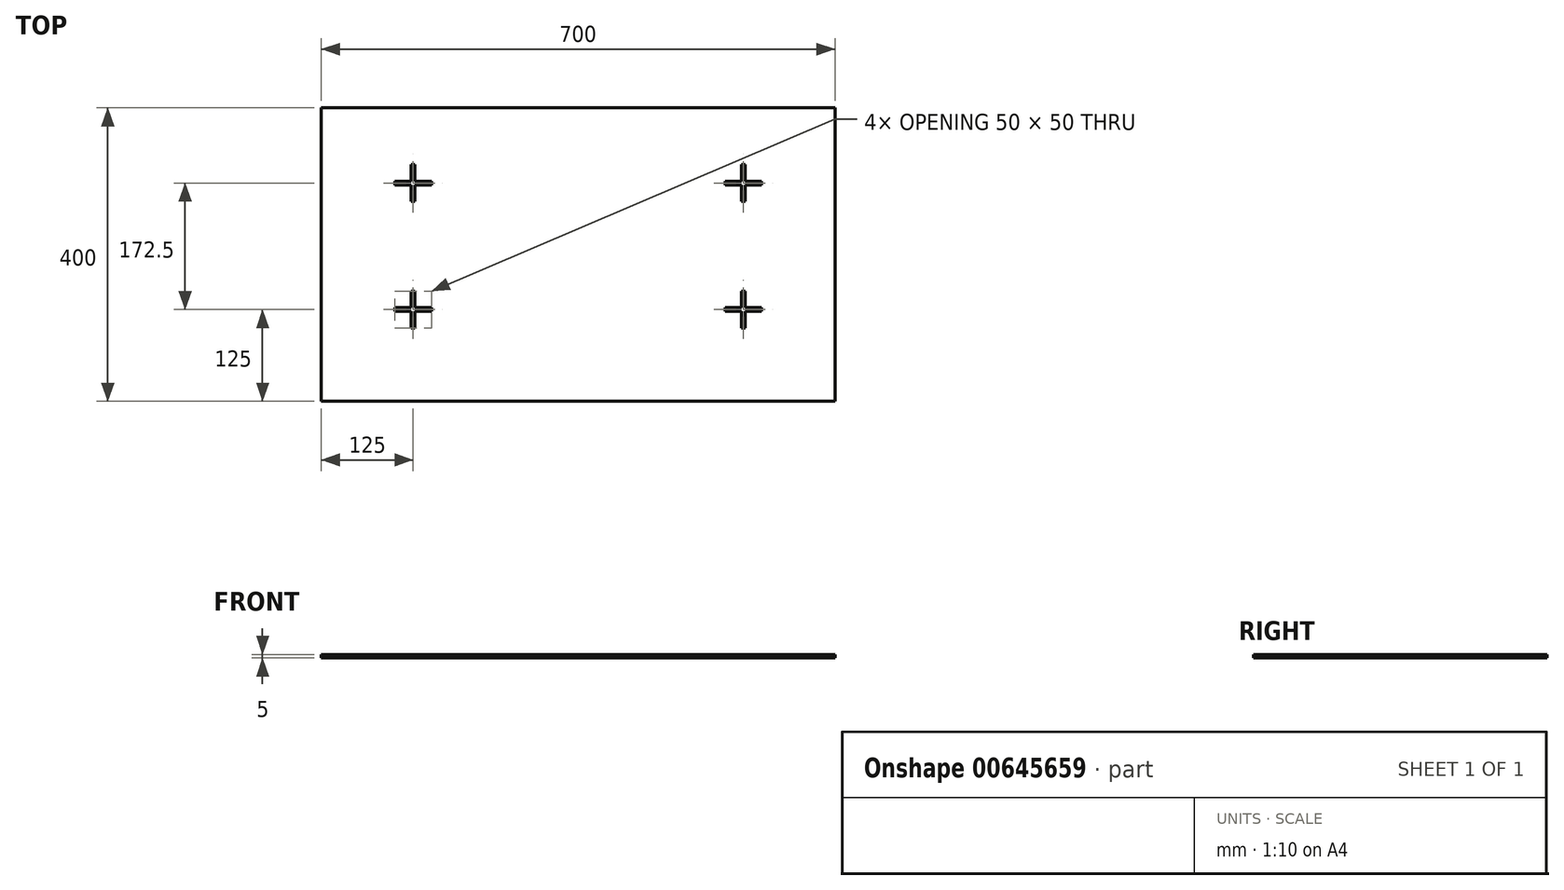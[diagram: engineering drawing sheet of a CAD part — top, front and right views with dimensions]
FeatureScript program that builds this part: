
annotation { "Feature Type Name" : "Feature", "Feature Type Description" : "" }
export const myFeature = defineFeature(function(context is Context, id is Id, definition is map)
    precondition{}
    {
        {
            var Q0;
            Q0=qCreatedBy(makeId("Top.planeOp"),FACE);
            var sketch = newSketch(context, id + "F0", { "sketchPlane" : qUnion([Q0])});
            skLineSegment(sketch, "E0.bottom", {"start": v(-700, 0) * mm, "end": v(0, 0) * mm});
            skLineSegment(sketch, "E0.top", {"start": v(-700, 400) * mm, "end": v(0, 400) * mm});
            skLineSegment(sketch, "E0.left", {"start": v(-700, 0) * mm, "end": v(-700, 400) * mm});
            skLineSegment(sketch, "E0.right", {"start": v(0, 0) * mm, "end": v(0, 400) * mm});
            skLineSegment(sketch, "E1", {"start": v(-600, 300) * mm, "end": v(-577.5, 300) * mm});
            skLineSegment(sketch, "E2", {"start": v(-577.5, 322.5) * mm, "end": v(-577.5, 300) * mm});
            skLineSegment(sketch, "E3", {"start": v(-577.5, 322.5) * mm, "end": v(-572.5, 322.5) * mm});
            skLineSegment(sketch, "E4", {"start": v(-572.5, 322.5) * mm, "end": v(-572.5, 300) * mm});
            skLineSegment(sketch, "E5", {"start": v(-572.5, 272.5) * mm, "end": v(-577.5, 272.5) * mm});
            skLineSegment(sketch, "E6", {"start": v(-600, 300) * mm, "end": v(-600, 295) * mm});
            skLineSegment(sketch, "E7", {"start": v(-600, 295) * mm, "end": v(-577.5, 295) * mm});
            skLineSegment(sketch, "E8", {"start": v(-550, 295) * mm, "end": v(-550, 300) * mm});
            skLineSegment(sketch, "E9.trimOffspring", {"start": v(-577.5, 295) * mm, "end": v(-577.5, 272.5) * mm});
            skLineSegment(sketch, "E10.trimOffspring", {"start": v(-572.5, 300) * mm, "end": v(-550, 300) * mm});
            skLineSegment(sketch, "E11.trimOffspring", {"start": v(-572.5, 295) * mm, "end": v(-572.5, 272.5) * mm});
            skLineSegment(sketch, "E12.trimOffspring", {"start": v(-572.5, 295) * mm, "end": v(-550, 295) * mm});
            skLineSegment(sketch, "E13", {"start": v(-600, 127.5) * mm, "end": v(-577.5, 127.5) * mm});
            skLineSegment(sketch, "E14", {"start": v(-577.5, 150) * mm, "end": v(-577.5, 127.5) * mm});
            skLineSegment(sketch, "E15", {"start": v(-577.5, 150) * mm, "end": v(-572.5, 150) * mm});
            skLineSegment(sketch, "E16", {"start": v(-572.5, 150) * mm, "end": v(-572.5, 127.5) * mm});
            skLineSegment(sketch, "E17", {"start": v(-572.5, 100) * mm, "end": v(-577.5, 100) * mm});
            skLineSegment(sketch, "E18", {"start": v(-600, 127.5) * mm, "end": v(-600, 122.5) * mm});
            skLineSegment(sketch, "E19", {"start": v(-600, 122.5) * mm, "end": v(-577.5, 122.5) * mm});
            skLineSegment(sketch, "E20", {"start": v(-550, 122.5) * mm, "end": v(-550, 127.5) * mm});
            skLineSegment(sketch, "E21.trimOffspring", {"start": v(-577.5, 122.5) * mm, "end": v(-577.5, 100) * mm});
            skLineSegment(sketch, "E22.trimOffspring", {"start": v(-572.5, 127.5) * mm, "end": v(-550, 127.5) * mm});
            skLineSegment(sketch, "E23.trimOffspring", {"start": v(-572.5, 122.5) * mm, "end": v(-572.5, 100) * mm});
            skLineSegment(sketch, "E24.trimOffspring", {"start": v(-572.5, 122.5) * mm, "end": v(-550, 122.5) * mm});
            skLineSegment(sketch, "E25", {"start": v(-150, 300) * mm, "end": v(-127.5, 300) * mm});
            skLineSegment(sketch, "E26", {"start": v(-127.5, 322.5) * mm, "end": v(-127.5, 300) * mm});
            skLineSegment(sketch, "E27", {"start": v(-127.5, 322.5) * mm, "end": v(-122.5, 322.5) * mm});
            skLineSegment(sketch, "E28", {"start": v(-122.5, 322.5) * mm, "end": v(-122.5, 300) * mm});
            skLineSegment(sketch, "E29", {"start": v(-122.5, 272.5) * mm, "end": v(-127.5, 272.5) * mm});
            skLineSegment(sketch, "E30", {"start": v(-150, 300) * mm, "end": v(-150, 295) * mm});
            skLineSegment(sketch, "E31", {"start": v(-150, 295) * mm, "end": v(-127.5, 295) * mm});
            skLineSegment(sketch, "E32", {"start": v(-100, 295) * mm, "end": v(-100, 300) * mm});
            skLineSegment(sketch, "E33.trimOffspring", {"start": v(-127.5, 295) * mm, "end": v(-127.5, 272.5) * mm});
            skLineSegment(sketch, "E34.trimOffspring", {"start": v(-122.5, 300) * mm, "end": v(-100, 300) * mm});
            skLineSegment(sketch, "E35.trimOffspring", {"start": v(-122.5, 295) * mm, "end": v(-122.5, 272.5) * mm});
            skLineSegment(sketch, "E36.trimOffspring", {"start": v(-122.5, 295) * mm, "end": v(-100, 295) * mm});
            skLineSegment(sketch, "E37", {"start": v(-150, 127.5) * mm, "end": v(-127.5, 127.5) * mm});
            skLineSegment(sketch, "E38", {"start": v(-127.5, 150) * mm, "end": v(-127.5, 127.5) * mm});
            skLineSegment(sketch, "E39", {"start": v(-127.5, 150) * mm, "end": v(-122.5, 150) * mm});
            skLineSegment(sketch, "E40", {"start": v(-122.5, 150) * mm, "end": v(-122.5, 127.5) * mm});
            skLineSegment(sketch, "E41", {"start": v(-122.5, 100) * mm, "end": v(-127.5, 100) * mm});
            skLineSegment(sketch, "E42", {"start": v(-150, 127.5) * mm, "end": v(-150, 122.5) * mm});
            skLineSegment(sketch, "E43", {"start": v(-150, 122.5) * mm, "end": v(-127.5, 122.5) * mm});
            skLineSegment(sketch, "E44", {"start": v(-100, 122.5) * mm, "end": v(-100, 127.5) * mm});
            skLineSegment(sketch, "E45.trimOffspring", {"start": v(-127.5, 122.5) * mm, "end": v(-127.5, 100) * mm});
            skLineSegment(sketch, "E46.trimOffspring", {"start": v(-122.5, 127.5) * mm, "end": v(-100, 127.5) * mm});
            skLineSegment(sketch, "E47.trimOffspring", {"start": v(-122.5, 122.5) * mm, "end": v(-122.5, 100) * mm});
            skLineSegment(sketch, "E48.trimOffspring", {"start": v(-122.5, 122.5) * mm, "end": v(-100, 122.5) * mm});
            skSolve(sketch);
        }
        {
            var Q0;
            Q0=makeQuery(id+"F0.imprint","IMPRINT",FACE,{"disambiguationData":[TD([[makeQuery(id+"F0.imprint","IMPRINT",EDGE,{"derivedFrom":sQuery(id+"F0.wireOp",EDGE,"E0.bottom")}),1.0]])]});
            extrude(context, id + "F1", {"entities" : qUnion([Q0]), "depth" : 5 * mm, "offsetDistance" : 25 * mm});
        }
    });
